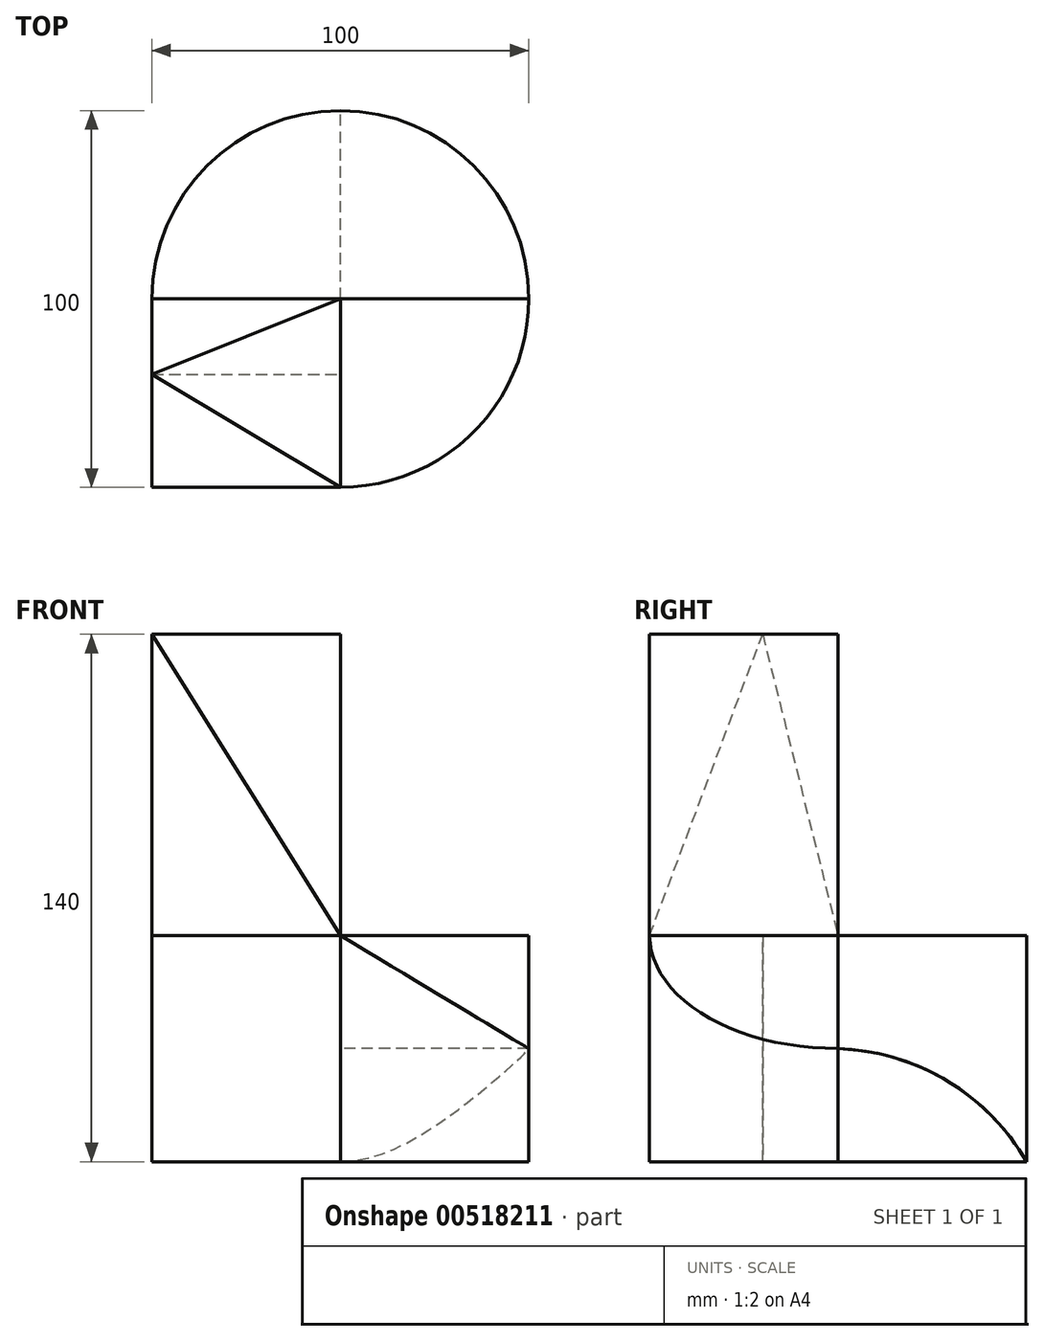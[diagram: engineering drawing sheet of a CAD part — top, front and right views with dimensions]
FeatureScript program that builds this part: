
annotation { "Feature Type Name" : "Feature", "Feature Type Description" : "" }
export const myFeature = defineFeature(function(context is Context, id is Id, definition is map)
    precondition{}
    {
        {
            var Q0;
            Q0=qCreatedBy(makeId("Top.planeOp"),FACE);
            var sketch = newSketch(context, id + "F0", { "sketchPlane" : qUnion([Q0])});
            skLineSegment(sketch, "E0.bottom", {"start": v(0, 0) * mm, "end": v(50, 0) * mm});
            skLineSegment(sketch, "E0.top", {"start": v(0, 50) * mm, "end": v(50, 50) * mm});
            skLineSegment(sketch, "E0.left", {"start": v(0, 0) * mm, "end": v(0, 50) * mm});
            skLineSegment(sketch, "E0.right", {"start": v(50, 0) * mm, "end": v(50, 50) * mm});
            skSolve(sketch);
        }
        {
            var Q0;
            Q0 = qSketchRegion(id + "F0", true);
            extrude(context, id + "F1", {"entities" : qUnion([Q0]), "depth" : 60 * mm, "offsetDistance" : 25 * mm});
        }
        {
            var Q0;
            Q0=makeQuery(id+"F1.opExtrude","SWEPT_FACE",FACE,{"disambiguationData":[OSD([sQuery(id+"F0.wireOp",EDGE,"E0.right")])]});
            var Q1;
            Q1=makeQuery(id+"F1.opExtrude","SWEPT_EDGE",EDGE,{"disambiguationData":[OSD([sQuery(id+"F0.wireOp",EDGE,"E0.top"),sQuery(id+"F0.wireOp",EDGE,"E0.right")])]});
            revolve(context, id + "F2", {"operationType" : NewBodyOperationType.ADD, "entities" : qUnion([Q0]), "axis" : qUnion([Q1]), "revolveType" : RevolveType.FULL});
        }
        {
            var Q0;
            Q0 = qSketchRegion(id + "F0", true);
            extrude(context, id + "F3", {"entities" : qUnion([Q0]), "operationType" : NewBodyOperationType.ADD, "depth" : 140 * mm, "offsetDistance" : 25 * mm});
        }
        {
            var Q0;
            {var subQ0=sQuery(id+"F0.wireOp",EDGE,"E0.bottom");Q0=makeQuery(id+"F3.boolean.opBoolean","MERGE",FACE,{"derivedFrom":[makeQuery(id+"F1.opExtrude","SWEPT_FACE",FACE,{"disambiguationData":[OSD([subQ0])]}),makeQuery(id+"F3.opExtrude","SWEPT_FACE",FACE,{"disambiguationData":[OSD([subQ0])]})]});}
            var sketch = newSketch(context, id + "F4", { "sketchPlane" : qUnion([Q0])});
            skLineSegment(sketch, "E1.bottom", {"start": v(0, 0) * mm, "end": v(50, 0) * mm});
            skLineSegment(sketch, "E1.top", {"start": v(0, 60) * mm, "end": v(50, 60) * mm});
            skLineSegment(sketch, "E1.left", {"start": v(0, 0) * mm, "end": v(0, 60) * mm});
            skLineSegment(sketch, "E1.right", {"start": v(50, 0) * mm, "end": v(50, 60) * mm});
            skSolve(sketch);
        }
        {
            var Q0;
            Q0=makeQuery(id+"F4.imprint","IMPRINT",FACE,{"disambiguationData":[TD([[makeQuery(id+"F4.imprint","IMPRINT",EDGE,{"derivedFrom":sQuery(id+"F4.wireOp",EDGE,"E1.bottom")}),1.0]])]});
            extrude(context, id + "F5", {"entities" : qUnion([Q0]), "operationType" : NewBodyOperationType.REMOVE, "oppositeDirection" : true, "depth" : 30 * mm, "offsetDistance" : 25 * mm});
        }
        {
            var Q0;
            Q0=makeQuery(id+"F3.opExtrude","CAP_FACE",FACE,{"disambiguationData":[OSD([sQuery(id+"F0.wireOp",EDGE,"E0.bottom"),sQuery(id+"F0.wireOp",EDGE,"E0.top"),sQuery(id+"F0.wireOp",EDGE,"E0.left"),sQuery(id+"F0.wireOp",EDGE,"E0.right")])],"isStart":false});
            var sketch = newSketch(context, id + "F6", { "sketchPlane" : qUnion([Q0])});
            skLineSegment(sketch, "E2", {"start": v(50, 0) * mm, "end": v(0, 30) * mm});
            skLineSegment(sketch, "E3", {"start": v(0, 30) * mm, "end": v(0, 0) * mm});
            skLineSegment(sketch, "E4", {"start": v(0, 0) * mm, "end": v(0, 30) * mm});
            skLineSegment(sketch, "E5", {"start": v(50, 50) * mm, "end": v(0, 30) * mm});
            skSolve(sketch);
        }
        {
            var Q1;
            {var subQ0=sQuery(id+"F0.wireOp",EDGE,"E0.bottom");Q1=makeQuery(id+"F3.boolean.opBoolean","MERGE",FACE,{"derivedFrom":[makeQuery(id+"F1.opExtrude","SWEPT_FACE",FACE,{"disambiguationData":[OSD([subQ0])]}),makeQuery(id+"F3.opExtrude","SWEPT_FACE",FACE,{"disambiguationData":[OSD([subQ0])]})]});}
            var Q2;
            Q2=sQuery(id+"F6.wireOp",VERTEX,"E5.end");
            loft(context, id + "F7", {"operationType" : NewBodyOperationType.REMOVE, "sheetProfilesArray" : [{ "sheetProfileEntities" : qUnion([Q1]) }, { "sheetProfileEntities" : qUnion([Q2]) }]});
        }
        {
            var Q1;
            {var subQ0=sQuery(id+"F6.wireOp",EDGE,"E5");Q1=makeQuery(id+"F6.imprint","IMPRINT",FACE,{"disambiguationData":[TD([[makeQuery(id+"F6.imprint","IMPRINT",EDGE,{"derivedFrom":subQ0}),-1.0]])]});}
            var Q2;
            {var subQ0=sQuery(id+"F0.wireOp",EDGE,"E0.right");var subQ1=sQuery(id+"F0.wireOp",EDGE,"E0.top");Q2=makeQuery(id+"F3.boolean.opBoolean","INTERSECT",VERTEX,{"derivedFrom":[makeQuery(id+"F2.boolean.opBoolean","MERGE",FACE,{"derivedFrom":[makeQuery(id+"F1.opExtrude","CAP_FACE",FACE,{"disambiguationData":[OSD([sQuery(id+"F0.wireOp",EDGE,"E0.bottom"),subQ1,sQuery(id+"F0.wireOp",EDGE,"E0.left"),subQ0])],"isStart":false}),makeQuery(id+"F2.opRevolve","SWEPT_FACE",FACE,{"disambiguationData":[OSD([subQ0]),TDD([makeQuery(id+"F1.opExtrude","CAP_EDGE",EDGE,{"disambiguationData":[OSD([subQ0])],"isStart":false})])]})]}),makeQuery(id+"F3.opExtrude","SWEPT_FACE",FACE,{"disambiguationData":[OSD([subQ1])]}),makeQuery(id+"F3.opExtrude","SWEPT_FACE",FACE,{"disambiguationData":[OSD([subQ0])]})]});}
            loft(context, id + "F8", {"operationType" : NewBodyOperationType.REMOVE, "sheetProfilesArray" : [{ "sheetProfileEntities" : qUnion([Q1]) }, { "sheetProfileEntities" : qUnion([Q2]) }]});
        }
        {
            var Q0;
            {var subQ0=sQuery(id+"F0.wireOp",EDGE,"E0.right");var subQ1=sQuery(id+"F0.wireOp",EDGE,"E0.left");var subQ2=sQuery(id+"F0.wireOp",EDGE,"E0.top");var subQ3=sQuery(id+"F0.wireOp",EDGE,"E0.bottom");Q0=makeQuery(id+"F8.boolean.opBoolean","MERGE",VERTEX,{"derivedFrom":[makeQuery(id+"F3.boolean.opBoolean","INTERSECT",VERTEX,{"derivedFrom":[makeQuery(id+"F2.boolean.opBoolean","MERGE",FACE,{"derivedFrom":[makeQuery(id+"F1.opExtrude","CAP_FACE",FACE,{"disambiguationData":[OSD([subQ3,subQ2,subQ1,subQ0])],"isStart":false}),makeQuery(id+"F2.opRevolve","SWEPT_FACE",FACE,{"disambiguationData":[OSD([subQ0]),TDD([makeQuery(id+"F1.opExtrude","CAP_EDGE",EDGE,{"disambiguationData":[OSD([subQ0])],"isStart":false})])]})]}),makeQuery(id+"F3.opExtrude","SWEPT_FACE",FACE,{"disambiguationData":[OSD([subQ2])]}),makeQuery(id+"F3.opExtrude","SWEPT_FACE",FACE,{"disambiguationData":[OSD([subQ0])]})]}),makeQuery(id+"F8.opLoft","SWEPT_VERTEX",VERTEX,{"disambiguationData":[OSD([subQ3,subQ2,subQ1,subQ0,sQuery(id+"F6.wireOp",EDGE,"E5")])]})]});}
            var Q1;
            {var subQ0=sQuery(id+"F0.wireOp",EDGE,"E0.right");var subQ1=sQuery(id+"F0.wireOp",EDGE,"E0.top");Q1=makeQuery(id+"F8.boolean.opBoolean","MERGE",VERTEX,{"derivedFrom":[makeQuery(id+"F3.opExtrude","CAP_VERTEX",VERTEX,{"disambiguationData":[OSD([subQ1,subQ0])],"isStart":false}),makeQuery(id+"F8.opLoft","MID_CAP_VERTEX",VERTEX,{"disambiguationData":[OSD([subQ1,subQ0,sQuery(id+"F6.wireOp",EDGE,"E5")])],"capPos":0.0})]});}
            var Q2;
            Q2=makeQuery(id+"F1.opExtrude","CAP_VERTEX",VERTEX,{"disambiguationData":[OSD([sQuery(id+"F0.wireOp",EDGE,"E0.top"),sQuery(id+"F0.wireOp",EDGE,"E0.left")])],"isStart":false});
            cPlane(context, id + "F9", {"entities" : qUnion([Q0, Q1, Q2]), "cplaneType" : CPlaneType.THREE_POINT, "offset" : 25 * mm, "width" : 150 * mm, "height" : 150 * mm});
        }
        {
            var Q0;
            Q0=qCreatedBy(id+"F9.planeOp",FACE);
            var sketch = newSketch(context, id + "F10", { "sketchPlane" : qUnion([Q0])});
            skLineSegment(sketch, "E6", {"start": v(-50, 60) * mm, "end": v(-100, 60) * mm});
            skLineSegment(sketch, "E7", {"start": v(-100, 60) * mm, "end": v(-100, 30) * mm});
            skLineSegment(sketch, "E8", {"start": v(-100, 30) * mm, "end": v(-50, 60) * mm});
            skSolve(sketch);
        }
        {
            var Q0;
            Q0 = qSketchRegion(id + "F10", true);
            extrude(context, id + "F11", {"entities" : qUnion([Q0]), "operationType" : NewBodyOperationType.REMOVE, "oppositeDirection" : true, "depth" : 126.1 * mm, "offsetDistance" : 25 * mm});
        }
        {
            var Q0;
            Q0=makeQuery(id+"F11.boolean.opBoolean","COPY",VERTEX,{"derivedFrom":makeQuery(id+"F11.opExtrude","CAP_VERTEX",VERTEX,{"disambiguationData":[OSD([sQuery(id+"F10.wireOp",EDGE,"E6"),sQuery(id+"F10.wireOp",EDGE,"E8")])],"isStart":true})});
            var Q1;
            Q1=makeQuery(id+"F11.boolean.opBoolean","INTERSECT",VERTEX,{"derivedFrom":[makeQuery(id+"F5.boolean.opBoolean","COPY",FACE,{"derivedFrom":makeQuery(id+"F5.opExtrude","SWEPT_FACE",FACE,{"disambiguationData":[OSD([sQuery(id+"F4.wireOp",EDGE,"E1.right")])]})}),makeQuery(id+"F2.opRevolve","SWEPT_FACE",FACE,{"disambiguationData":[OSD([sQuery(id+"F0.wireOp",EDGE,"E0.bottom"),sQuery(id+"F0.wireOp",EDGE,"E0.right")])]}),makeQuery(id+"F11.opExtrude","SWEPT_FACE",FACE,{"disambiguationData":[OSD([sQuery(id+"F10.wireOp",EDGE,"E8")])]})]});
            var Q2;
            Q2=makeQuery(id+"F5.boolean.opBoolean","COPY",VERTEX,{"derivedFrom":makeQuery(id+"F5.opExtrude","CAP_VERTEX",VERTEX,{"disambiguationData":[OSD([sQuery(id+"F4.wireOp",EDGE,"E1.bottom"),sQuery(id+"F4.wireOp",EDGE,"E1.right")])],"isStart":true})});
            cPlane(context, id + "F12", {"entities" : qUnion([Q0, Q1, Q2]), "cplaneType" : CPlaneType.THREE_POINT, "offset" : 25 * mm, "width" : 150 * mm, "height" : 150 * mm});
        }
        {
            var Q0;
            Q0=qCreatedBy(id+"F12.planeOp",FACE);
            var sketch = newSketch(context, id + "F13", { "sketchPlane" : qUnion([Q0])});
            skLineSegment(sketch, "E9", {"start": v(-50, 30) * mm, "end": v(-50, 0) * mm});
            skLineSegment(sketch, "E10", {"start": v(-50, 0) * mm, "end": v(-100, 0) * mm});
            skArc(sketch, "E11", {"start": v(-50, 30) * mm, "mid": v(-78.88, 21.48) * mm, "end": v(-100, 0) * mm});
            skSolve(sketch);
        }
        {
            var Q0;
            Q0 = qSketchRegion(id + "F13", true);
            extrude(context, id + "F14", {"entities" : qUnion([Q0]), "operationType" : NewBodyOperationType.REMOVE, "oppositeDirection" : true, "depth" : 64.1 * mm, "offsetDistance" : 25 * mm});
        }
    });
